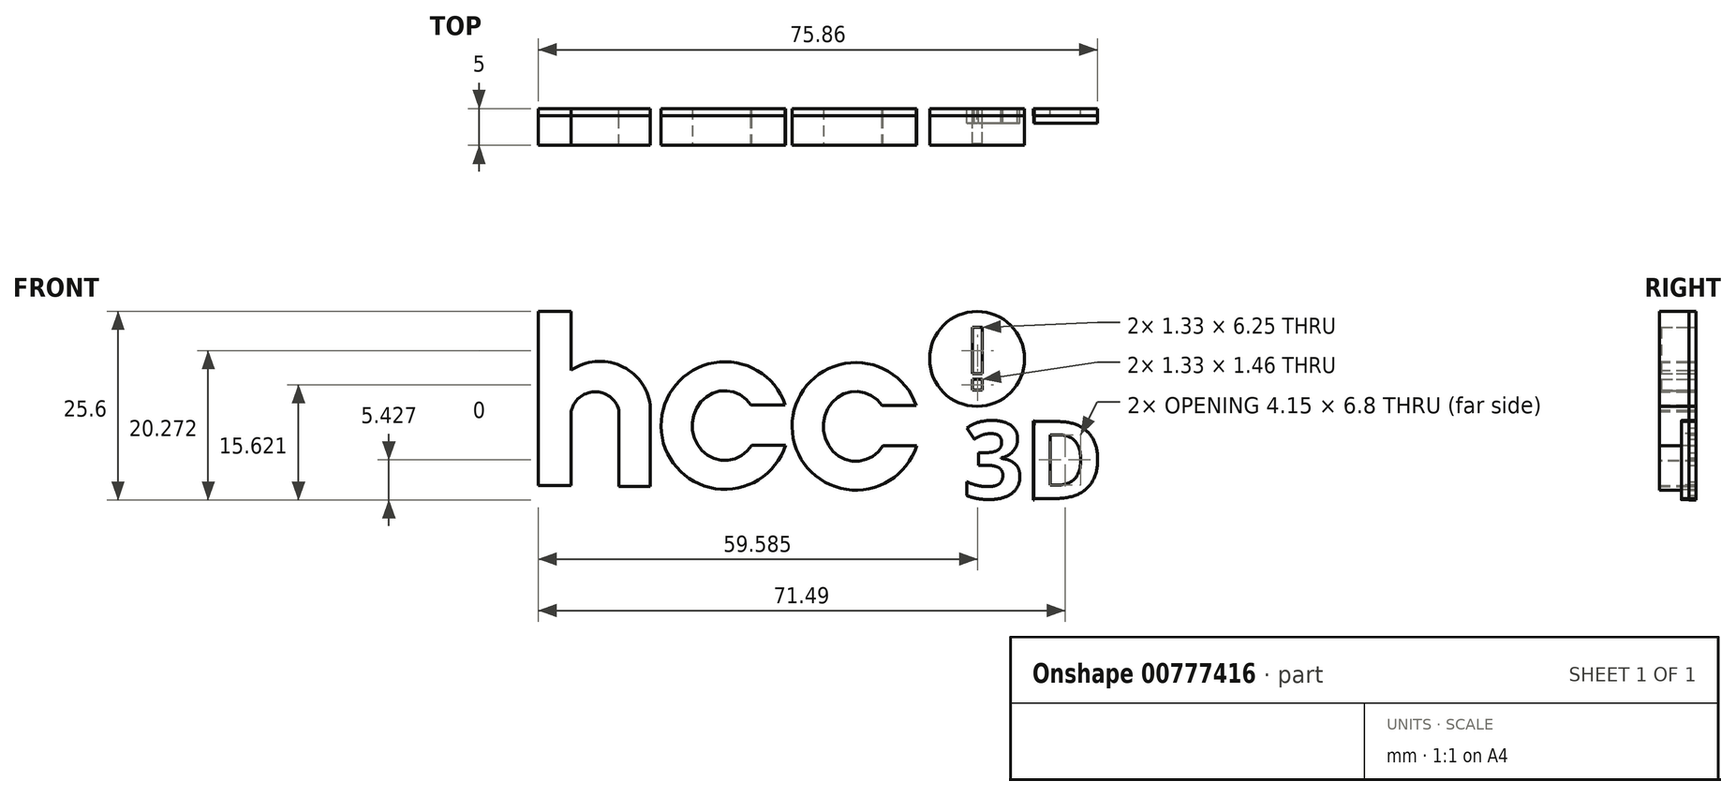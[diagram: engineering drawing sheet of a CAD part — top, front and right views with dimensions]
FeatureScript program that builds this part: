
annotation { "Feature Type Name" : "Feature", "Feature Type Description" : "" }
export const myFeature = defineFeature(function(context is Context, id is Id, definition is map)
    precondition{}
    {
        {
            var Q0;
            Q0=qCreatedBy(makeId("Front.planeOp"),FACE);
            var sketch = newSketch(context, id + "F0", { "sketchPlane" : qUnion([Q0])});
            skLineSegment(sketch, "E0.bottom", {"start": v(-29.23, 12.7) * mm, "end": v(-33.71, 12.7) * mm});
            skLineSegment(sketch, "E0.top", {"start": v(-29.23, -10.95) * mm, "end": v(-33.71, -10.95) * mm});
            skLineSegment(sketch, "E0.left", {"start": v(-29.23, 12.7) * mm, "end": v(-29.23, 4.68) * mm});
            skLineSegment(sketch, "E0.right", {"start": v(-33.71, 12.7) * mm, "end": v(-33.71, -10.95) * mm});
            skArc(sketch, "E1", {"start": v(-18.5, 0) * mm, "mid": v(-22.56, 5.32) * mm, "end": v(-29.23, 4.68) * mm});
            skArc(sketch, "E2", {"start": v(-22.75, -0.72) * mm, "mid": v(-26.08, 1.76) * mm, "end": v(-29.23, -0.94) * mm});
            skLineSegment(sketch, "E3", {"start": v(-22.75, -0.72) * mm, "end": v(-22.75, -11.06) * mm});
            skLineSegment(sketch, "E4", {"start": v(-22.75, -11.06) * mm, "end": v(-18.5, -11.06) * mm});
            skLineSegment(sketch, "E5", {"start": v(-18.5, -11.06) * mm, "end": v(-18.5, 0) * mm});
            skArc(sketch, "E6", {"start": v(-0.2, 0) * mm, "mid": v(-17.04, -2.91) * mm, "end": v(-0.14, -5.47) * mm});
            skEllipticalArc(sketch, "E7", {});
            skLineSegment(sketch, "E8", {"start": v(-4.83, 0) * mm, "end": v(0, 0) * mm});
            skLineSegment(sketch, "E9", {"start": v(-4.72, -5.47) * mm, "end": v(0, -5.47) * mm});
            skArc(sketch, "E10", {"start": v(17.56, -0.1) * mm, "mid": v(0.73, -3) * mm, "end": v(17.62, -5.56) * mm});
            skEllipticalArc(sketch, "E11", {});
            skLineSegment(sketch, "E12", {"start": v(12.93, -0.1) * mm, "end": v(17.76, -0.1) * mm});
            skLineSegment(sketch, "E13", {"start": v(13.05, -5.56) * mm, "end": v(17.76, -5.56) * mm});
            skCircle(sketch, "E14", {"center": v(25.8, 6.23) * mm, "radius": 6.44 * mm});
            skLineSegment(sketch, "E15.bottom", {"start": v(25.21, 10.49) * mm, "end": v(26.54, 10.49) * mm});
            skLineSegment(sketch, "E15.top", {"start": v(25.21, 4.24) * mm, "end": v(26.54, 4.24) * mm});
            skLineSegment(sketch, "E15.left", {"start": v(25.21, 10.49) * mm, "end": v(25.21, 4.24) * mm});
            skLineSegment(sketch, "E15.right", {"start": v(26.54, 10.49) * mm, "end": v(26.54, 4.24) * mm});
            skLineSegment(sketch, "E16.bottom", {"start": v(25.21, 3.44) * mm, "end": v(26.54, 3.44) * mm});
            skLineSegment(sketch, "E16.top", {"start": v(25.21, 1.98) * mm, "end": v(26.54, 1.98) * mm});
            skLineSegment(sketch, "E16.left", {"start": v(25.21, 3.44) * mm, "end": v(25.21, 1.98) * mm});
            skLineSegment(sketch, "E16.right", {"start": v(26.54, 3.44) * mm, "end": v(26.54, 1.98) * mm});
            skPoint(sketch, "E17.orphan", {"position": v(-32.13, 0) * mm});
            skLineSegment(sketch, "E18.trimOffspring", {"start": v(-29.23, -0.94) * mm, "end": v(-29.23, -10.95) * mm});
            skText(sketch, "E19", { "text": "3D", "fontName": "OpenSans-Bold.ttf"});
            skLineSegment(sketch, "E20.bottom", {"start": v(33.46, -2.18) * mm, "end": v(33.55, -2.18) * mm});
            skLineSegment(sketch, "E20.top", {"start": v(33.46, -2.18) * mm, "end": v(33.55, -2.18) * mm});
            skLineSegment(sketch, "E20.left", {"start": v(33.55, -2.18) * mm, "end": v(33.55, -2.18) * mm});
            skLineSegment(sketch, "E20.right", {"start": v(33.46, -2.18) * mm, "end": v(33.46, -2.18) * mm});
            skLineSegment(sketch, "E21.bottom", {"start": v(33.55, -12.71) * mm, "end": v(33.46, -12.71) * mm});
            skLineSegment(sketch, "E21.top", {"start": v(33.55, -12.91) * mm, "end": v(33.46, -12.91) * mm});
            skLineSegment(sketch, "E21.left", {"start": v(33.46, -12.91) * mm, "end": v(33.46, -12.71) * mm});
            skLineSegment(sketch, "E21.right", {"start": v(33.55, -12.91) * mm, "end": v(33.55, -12.71) * mm});
            skLineSegment(sketch, "E22.bottom", {"start": v(33.64, -12.71) * mm, "end": v(33.46, -12.71) * mm});
            skLineSegment(sketch, "E22.top", {"start": v(33.55, -2.18) * mm, "end": v(33.46, -2.18) * mm});
            skLineSegment(sketch, "E22.left", {"start": v(33.46, -12.71) * mm, "end": v(33.46, -2.18) * mm});
            skLineSegment(sketch, "E23.top", {"start": v(33.46, -2.76) * mm, "end": v(33.55, -2.76) * mm});
            skLineSegment(sketch, "E23.left", {"start": v(33.55, -2.18) * mm, "end": v(33.55, -2.76) * mm});
            skLineSegment(sketch, "E23.right", {"start": v(33.46, -2.18) * mm, "end": v(33.46, -2.76) * mm});
            skLineSegment(sketch, "E24.left", {"start": v(33.55, -3.88) * mm, "end": v(33.55, -12.94) * mm});
            skPoint(sketch, "E25.end.orphan", {"position": v(36.71, 0) * mm});
            skPoint(sketch, "E25.start.orphan", {"position": v(33.55, 0) * mm});
            const initialGuessF0  = {"E7": [-0.00838379468768835, -0.002821371890604496, 0, 1, 0.004734611138701439, 0.0044216665190650265, 5.350779379737523, 4.11952951118792], "E11": [0.009380069561302662, -0.0029154655057936907, 0, 1, 0.004734611138701439, 0.0044216665190650265, 5.350779379737523, 4.11952951118792], "E19": [0.02383, -0.01271, 1, 0, 0.01053]};
            skSetInitialGuess(sketch, initialGuessF0);
            skSolve(sketch);
        }
        {
            var Q0;
            Q0=makeQuery(id+"F0.imprint","IMPRINT",FACE,{"disambiguationData":[TD([[makeQuery(id+"F0.imprint","IMPRINT",EDGE,{"derivedFrom":sQuery(id+"F0.wireOp",EDGE,"E0.bottom")}),1.0]])]});
            var Q1;
            {var subQ0=sQuery(id+"F0.wireOp",EDGE,"E6");Q1=makeQuery(id+"F0.imprint","IMPRINT",FACE,{"disambiguationData":[TD([[makeQuery(id+"F0.imprint","IMPRINT",EDGE,{"derivedFrom":subQ0}),1.0]])]});}
            var Q2;
            {var subQ0=sQuery(id+"F0.wireOp",EDGE,"E10");Q2=makeQuery(id+"F0.imprint","IMPRINT",FACE,{"disambiguationData":[TD([[makeQuery(id+"F0.imprint","IMPRINT",EDGE,{"derivedFrom":subQ0}),1.0]])]});}
            extrude(context, id + "F1", {"entities" : qUnion([Q0, Q1, Q2]), "depth" : 5 * mm, "offsetDistance" : 25 * mm});
        }
        {
            var Q0;
            Q0=makeQuery(id+"F0.imprint","IMPRINT",FACE,{"disambiguationData":[TD([[makeQuery(id+"F0.imprint","IMPRINT",EDGE,{"derivedFrom":sQuery(id+"F0.wireOp",EDGE,"E14")}),1.0]])]});
            extrude(context, id + "F2", {"entities" : qUnion([Q0]), "depth" : 5 * mm, "offsetDistance" : 25 * mm});
        }
        {
            var Q0;
            Q0=makeQuery(id+"F0.imprint","IMPRINT",FACE,{"disambiguationData":[TD([[makeQuery(id+"F0.imprint","IMPRINT",EDGE,{"derivedFrom":sQuery(id+"F0.wireOp",EDGE,"E19.sketch_text.stroke-27")}),-1.0]])]});
            var Q1;
            Q1=makeQuery(id+"F0.imprint","IMPRINT",FACE,{"disambiguationData":[TD([[makeQuery(id+"F0.imprint","IMPRINT",EDGE,{"derivedFrom":sQuery(id+"F0.wireOp",EDGE,"E19.sketch_text.stroke-0")}),-1.0]])]});
            extrude(context, id + "F3", {"entities" : qUnion([Q0, Q1]), "depth" : 2 * mm, "offsetDistance" : 25 * mm});
        }
        {
            var Q0;
            Q0=makeQuery(id+"F0.imprint","IMPRINT",FACE,{"disambiguationData":[TD([[makeQuery(id+"F0.imprint","IMPRINT",EDGE,{"derivedFrom":sQuery(id+"F0.wireOp",EDGE,"E15.bottom")}),-1.0]])]});
            var Q1;
            Q1=makeQuery(id+"F0.imprint","IMPRINT",FACE,{"disambiguationData":[TD([[makeQuery(id+"F0.imprint","IMPRINT",EDGE,{"derivedFrom":sQuery(id+"F0.wireOp",EDGE,"E16.bottom")}),-1.0]])]});
            extrude(context, id + "F4", {"entities" : qUnion([Q0, Q1]), "depth" : 4.7 * mm, "offsetDistance" : 25 * mm});
        }
        {
            var Q0;
            Q0 = qSketchRegion(id + "F0", true);
            extrude(context, id + "F5", {"entities" : qUnion([Q0]), "depth" : 1 * mm, "offsetDistance" : 25 * mm});
        }
    });
